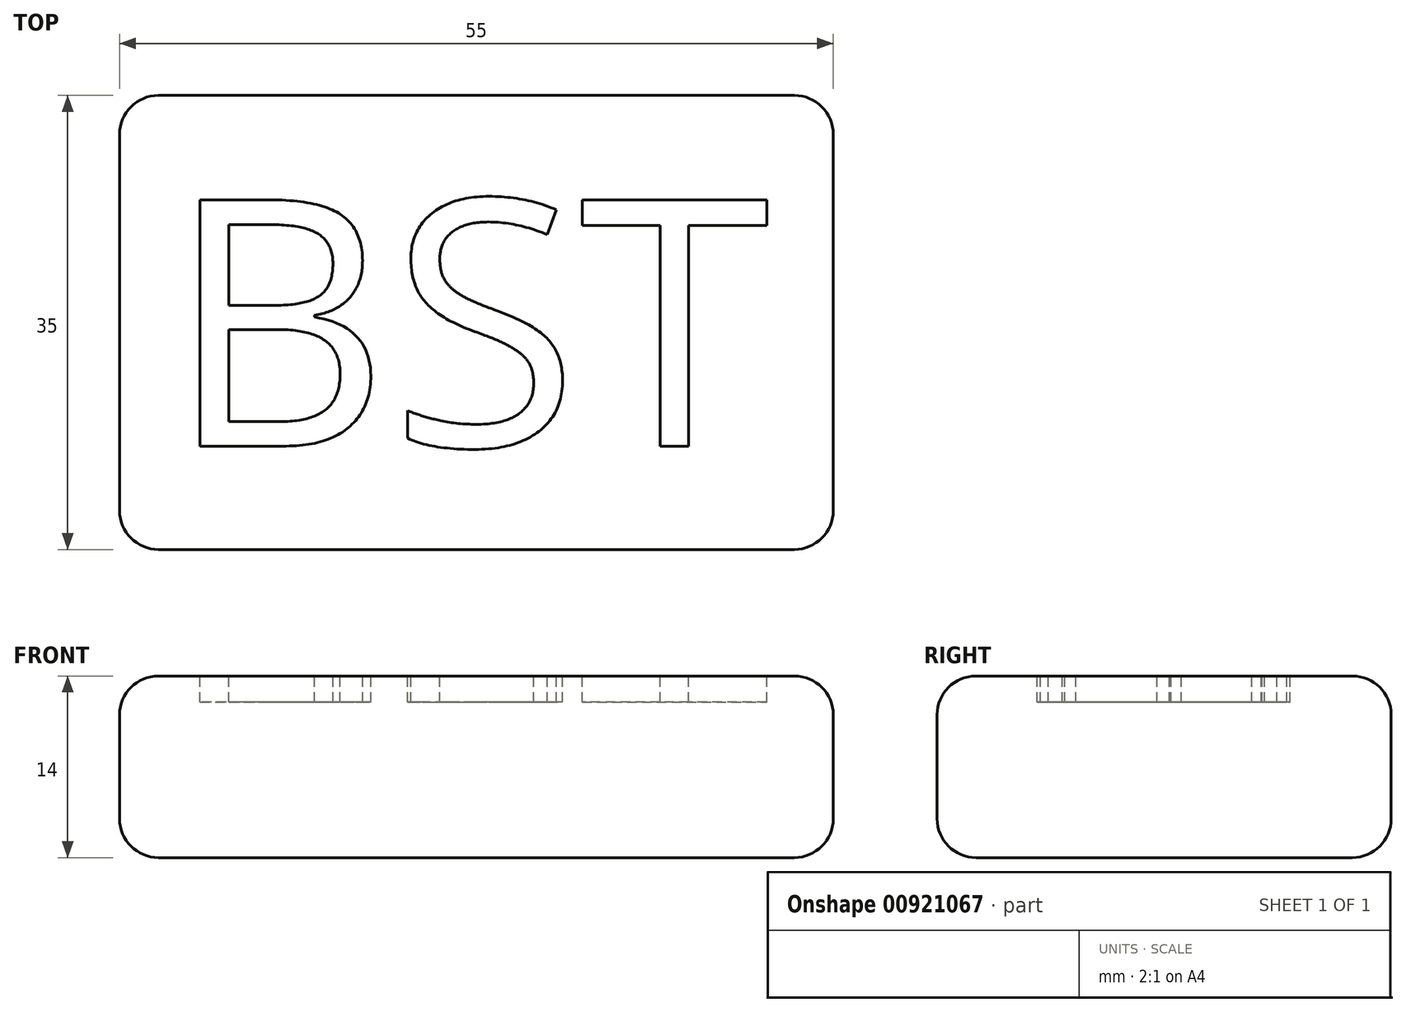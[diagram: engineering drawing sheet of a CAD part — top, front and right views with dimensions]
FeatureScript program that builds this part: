
annotation { "Feature Type Name" : "Feature", "Feature Type Description" : "" }
export const myFeature = defineFeature(function(context is Context, id is Id, definition is map)
    precondition{}
    {
        {
            var Q0;
            Q0=qCreatedBy(makeId("Top.planeOp"),FACE);
            var sketch = newSketch(context, id + "F0", { "sketchPlane" : qUnion([Q0])});
            skLineSegment(sketch, "E0.bottom", {"start": v(-27.5, 17.5) * mm, "end": v(27.5, 17.5) * mm});
            skLineSegment(sketch, "E0.top", {"start": v(-27.5, -17.5) * mm, "end": v(27.5, -17.5) * mm});
            skLineSegment(sketch, "E0.left", {"start": v(-27.5, 17.5) * mm, "end": v(-27.5, -17.5) * mm});
            skLineSegment(sketch, "E0.right", {"start": v(27.5, 17.5) * mm, "end": v(27.5, -17.5) * mm});
            skPoint(sketch, "E0.middle", {"position": v(0, 0) * mm});
            skSolve(sketch);
        }
        {
            var Q0;
            Q0=makeQuery(id+"F0.imprint","IMPRINT",FACE,{"disambiguationData":[TD([[makeQuery(id+"F0.imprint","IMPRINT",EDGE,{"derivedFrom":sQuery(id+"F0.wireOp",EDGE,"E0.bottom")}),-1.0]])]});
            extrude(context, id + "F1", {"entities" : qUnion([Q0]), "depth" : 14 * mm, "offsetDistance" : 25 * mm});
        }
        {
            var Q0;
            Q0=makeQuery(id+"F1.opExtrude","CAP_EDGE",EDGE,{"disambiguationData":[OSD([sQuery(id+"F0.wireOp",EDGE,"E0.bottom")])],"isStart":false});
            var Q1;
            Q1=makeQuery(id+"F1.opExtrude","CAP_EDGE",EDGE,{"disambiguationData":[OSD([sQuery(id+"F0.wireOp",EDGE,"E0.top")])],"isStart":false});
            var Q2;
            Q2=makeQuery(id+"F1.opExtrude","CAP_EDGE",EDGE,{"disambiguationData":[OSD([sQuery(id+"F0.wireOp",EDGE,"E0.right")])],"isStart":false});
            var Q3;
            Q3=makeQuery(id+"F1.opExtrude","CAP_FACE",FACE,{"disambiguationData":[OSD([sQuery(id+"F0.wireOp",EDGE,"E0.bottom"),sQuery(id+"F0.wireOp",EDGE,"E0.top"),sQuery(id+"F0.wireOp",EDGE,"E0.left"),sQuery(id+"F0.wireOp",EDGE,"E0.right")])],"isStart":false});
            var Q4;
            Q4=makeQuery(id+"F1.opExtrude","CAP_EDGE",EDGE,{"disambiguationData":[OSD([sQuery(id+"F0.wireOp",EDGE,"E0.top")])],"isStart":true});
            var Q5;
            Q5=makeQuery(id+"F1.opExtrude","CAP_EDGE",EDGE,{"disambiguationData":[OSD([sQuery(id+"F0.wireOp",EDGE,"E0.bottom")])],"isStart":true});
            var Q6;
            Q6=makeQuery(id+"F1.opExtrude","CAP_EDGE",EDGE,{"disambiguationData":[OSD([sQuery(id+"F0.wireOp",EDGE,"E0.left")])],"isStart":true});
            var Q7;
            Q7=makeQuery(id+"F1.opExtrude","CAP_EDGE",EDGE,{"disambiguationData":[OSD([sQuery(id+"F0.wireOp",EDGE,"E0.right")])],"isStart":true});
            var Q8;
            Q8=makeQuery(id+"F1.opExtrude","SWEPT_EDGE",EDGE,{"disambiguationData":[OSD([sQuery(id+"F0.wireOp",EDGE,"E0.top"),sQuery(id+"F0.wireOp",EDGE,"E0.left")])]});
            var Q9;
            Q9=makeQuery(id+"F1.opExtrude","SWEPT_EDGE",EDGE,{"disambiguationData":[OSD([sQuery(id+"F0.wireOp",EDGE,"E0.top"),sQuery(id+"F0.wireOp",EDGE,"E0.right")])]});
            var Q10;
            Q10=makeQuery(id+"F1.opExtrude","SWEPT_EDGE",EDGE,{"disambiguationData":[OSD([sQuery(id+"F0.wireOp",EDGE,"E0.bottom"),sQuery(id+"F0.wireOp",EDGE,"E0.right")])]});
            var Q11;
            Q11=makeQuery(id+"F1.opExtrude","SWEPT_EDGE",EDGE,{"disambiguationData":[OSD([sQuery(id+"F0.wireOp",EDGE,"E0.bottom"),sQuery(id+"F0.wireOp",EDGE,"E0.left")])]});
            fillet(context, id + "F2", {"entities" : qUnion([Q0, Q1, Q2, Q3, Q4, Q5, Q6, Q7, Q8, Q9, Q10, Q11]), "radius" : 3 * mm, "tangentPropagation" : true, "allowEdgeOverflow" : false});
        }
        {
            var Q0;
            Q0=qCreatedBy(makeId("Top.planeOp"),FACE);
            cPlane(context, id + "F3", {"entities" : qUnion([Q0]), "cplaneType" : CPlaneType.OFFSET, "offset" : 14 * mm, "width" : 150 * mm, "height" : 150 * mm});
        }
        {
            var Q0;
            Q0=qCreatedBy(id+"F3.planeOp",FACE);
            var sketch = newSketch(context, id + "F4", { "sketchPlane" : qUnion([Q0])});
            skText(sketch, "E1", { "text": "BST", "fontName": "OpenSans-Regular.ttf"});
            const initialGuessF4  = {"E1": [-0.0239, -0.00953, 1, 0, 0.01914]};
            skSetInitialGuess(sketch, initialGuessF4);
            skSolve(sketch);
        }
        {
            var Q0;
            Q0 = qSketchRegion(id + "F4", true);
            extrude(context, id + "F5", {"entities" : qUnion([Q0]), "operationType" : NewBodyOperationType.REMOVE, "oppositeDirection" : true, "depth" : 2 * mm, "offsetDistance" : 25 * mm});
        }
    });
